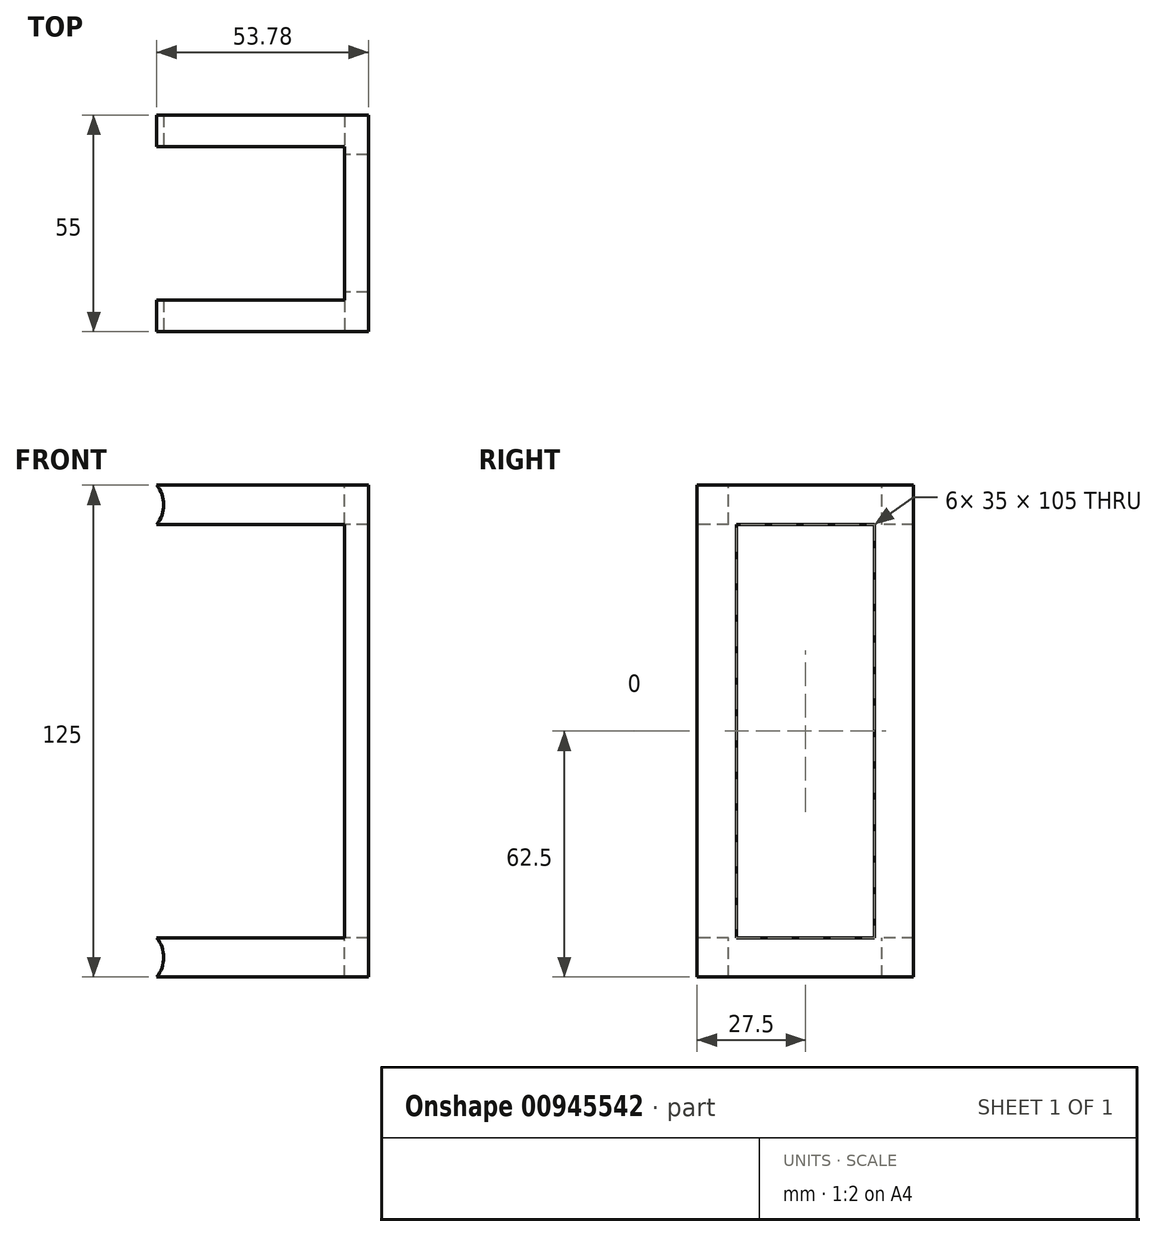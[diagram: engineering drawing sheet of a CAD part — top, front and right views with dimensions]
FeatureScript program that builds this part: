
annotation { "Feature Type Name" : "Feature", "Feature Type Description" : "" }
export const myFeature = defineFeature(function(context is Context, id is Id, definition is map)
    precondition{}
    {
        {
            var Q0;
            Q0=qCreatedBy(makeId("Front.planeOp"),FACE);
            var sketch = newSketch(context, id + "F0", { "sketchPlane" : qUnion([Q0])});
            skLineSegment(sketch, "E0.bottom", {"start": v(-39.57, 62.5) * mm, "end": v(20.43, 62.5) * mm});
            skLineSegment(sketch, "E0.top", {"start": v(-39.57, -62.5) * mm, "end": v(20.43, -62.5) * mm});
            skLineSegment(sketch, "E0.left", {"start": v(-39.57, 62.5) * mm, "end": v(-39.57, -62.5) * mm});
            skLineSegment(sketch, "E0.right", {"start": v(20.43, 62.5) * mm, "end": v(20.43, -62.5) * mm});
            skSolve(sketch);
        }
        {
            var Q0;
            Q0 = qSketchRegion(id + "F0", true);
            extrude(context, id + "F1", {"entities" : qUnion([Q0]), "depth" : 55 * mm, "offsetDistance" : 25 * mm});
        }
        {
            var Q0;
            Q0=makeQuery(id+"F1.opExtrude","CAP_FACE",FACE,{"disambiguationData":[OSD([sQuery(id+"F0.wireOp",EDGE,"E0.bottom"),sQuery(id+"F0.wireOp",EDGE,"E0.top"),sQuery(id+"F0.wireOp",EDGE,"E0.left"),sQuery(id+"F0.wireOp",EDGE,"E0.right")])],"isStart":false});
            var sketch = newSketch(context, id + "F2", { "sketchPlane" : qUnion([Q0])});
            skLineSegment(sketch, "E1.bottom", {"start": v(-39.57, 52.5) * mm, "end": v(14.43, 52.5) * mm});
            skLineSegment(sketch, "E1.top", {"start": v(-39.57, -52.5) * mm, "end": v(14.43, -52.5) * mm});
            skLineSegment(sketch, "E1.left", {"start": v(-39.57, 52.5) * mm, "end": v(-39.57, -52.5) * mm});
            skLineSegment(sketch, "E1.right", {"start": v(14.43, 52.5) * mm, "end": v(14.43, -52.5) * mm});
            skSolve(sketch);
        }
        {
            var Q0;
            Q0 = qSketchRegion(id + "F2", true);
            extrude(context, id + "F3", {"entities" : qUnion([Q0]), "operationType" : NewBodyOperationType.REMOVE, "endBound" : BoundingType.THROUGH_ALL, "oppositeDirection" : true, "depth" : 25 * mm, "offsetDistance" : 25 * mm});
        }
        {
            var Q0;
            Q0=makeQuery(id+"F1.opExtrude","CAP_FACE",FACE,{"disambiguationData":[OSD([sQuery(id+"F0.wireOp",EDGE,"E0.bottom"),sQuery(id+"F0.wireOp",EDGE,"E0.top"),sQuery(id+"F0.wireOp",EDGE,"E0.left"),sQuery(id+"F0.wireOp",EDGE,"E0.right")])],"isStart":false});
            var sketch = newSketch(context, id + "F4", { "sketchPlane" : qUnion([Q0])});
            skCircle(sketch, "E2", {"center": v(-39.57, 57.5) * mm, "radius": 7.98 * mm});
            skLineSegment(sketch, "E3", {"start": v(-56.09, 0) * mm, "end": v(32.03, 0) * mm, "construction": true});
            skCircle(sketch, "E4.MirrorC", {"center": v(-39.57, -57.5) * mm, "radius": 7.98 * mm});
            skSolve(sketch);
        }
        {
            var Q0;
            Q0 = qSketchRegion(id + "F4", true);
            extrude(context, id + "F5", {"entities" : qUnion([Q0]), "operationType" : NewBodyOperationType.REMOVE, "endBound" : BoundingType.THROUGH_ALL, "oppositeDirection" : true, "depth" : 25 * mm, "offsetDistance" : 25 * mm});
        }
        {
            var Q0;
            Q0=makeQuery(id+"F1.opExtrude","SWEPT_FACE",FACE,{"disambiguationData":[OSD([sQuery(id+"F0.wireOp",EDGE,"E0.bottom")])]});
            var sketch = newSketch(context, id + "F6", { "sketchPlane" : qUnion([Q0])});
            skLineSegment(sketch, "E5.bottom", {"start": v(-33.35, -8) * mm, "end": v(14.43, -8) * mm});
            skLineSegment(sketch, "E5.top", {"start": v(-33.35, -47) * mm, "end": v(14.43, -47) * mm});
            skLineSegment(sketch, "E5.left", {"start": v(-33.35, -8) * mm, "end": v(-33.35, -47) * mm});
            skLineSegment(sketch, "E5.right", {"start": v(14.43, -8) * mm, "end": v(14.43, -47) * mm});
            skSolve(sketch);
        }
        {
            var Q0;
            Q0 = qSketchRegion(id + "F6", true);
            extrude(context, id + "F7", {"entities" : qUnion([Q0]), "operationType" : NewBodyOperationType.REMOVE, "endBound" : BoundingType.THROUGH_ALL, "oppositeDirection" : true, "depth" : 25 * mm, "offsetDistance" : 25 * mm});
        }
        {
            var Q0;
            Q0=makeQuery(id+"F7.boolean.opBoolean","MERGE",FACE,{"derivedFrom":[makeQuery(id+"F3.boolean.opBoolean","COPY",FACE,{"derivedFrom":makeQuery(id+"F3.opExtrude","SWEPT_FACE",FACE,{"disambiguationData":[OSD([sQuery(id+"F2.wireOp",EDGE,"E1.right")])]})})],"fromTools":[makeQuery(id+"F7.opExtrude","SWEPT_FACE",FACE,{"disambiguationData":[OSD([sQuery(id+"F6.wireOp",EDGE,"E5.right")])]})]});
            var sketch = newSketch(context, id + "F8", { "sketchPlane" : qUnion([Q0])});
            skLineSegment(sketch, "E6.bottom", {"start": v(10, 52.5) * mm, "end": v(45, 52.5) * mm});
            skLineSegment(sketch, "E6.top", {"start": v(10, -52.5) * mm, "end": v(45, -52.5) * mm});
            skLineSegment(sketch, "E6.left", {"start": v(10, 52.5) * mm, "end": v(10, -52.5) * mm});
            skLineSegment(sketch, "E6.right", {"start": v(45, 52.5) * mm, "end": v(45, -52.5) * mm});
            skSolve(sketch);
        }
        {
            var Q0;
            Q0 = qSketchRegion(id + "F8", true);
            extrude(context, id + "F9", {"entities" : qUnion([Q0]), "operationType" : NewBodyOperationType.REMOVE, "endBound" : BoundingType.THROUGH_ALL, "oppositeDirection" : true, "depth" : 25 * mm, "offsetDistance" : 25 * mm});
        }
    });
